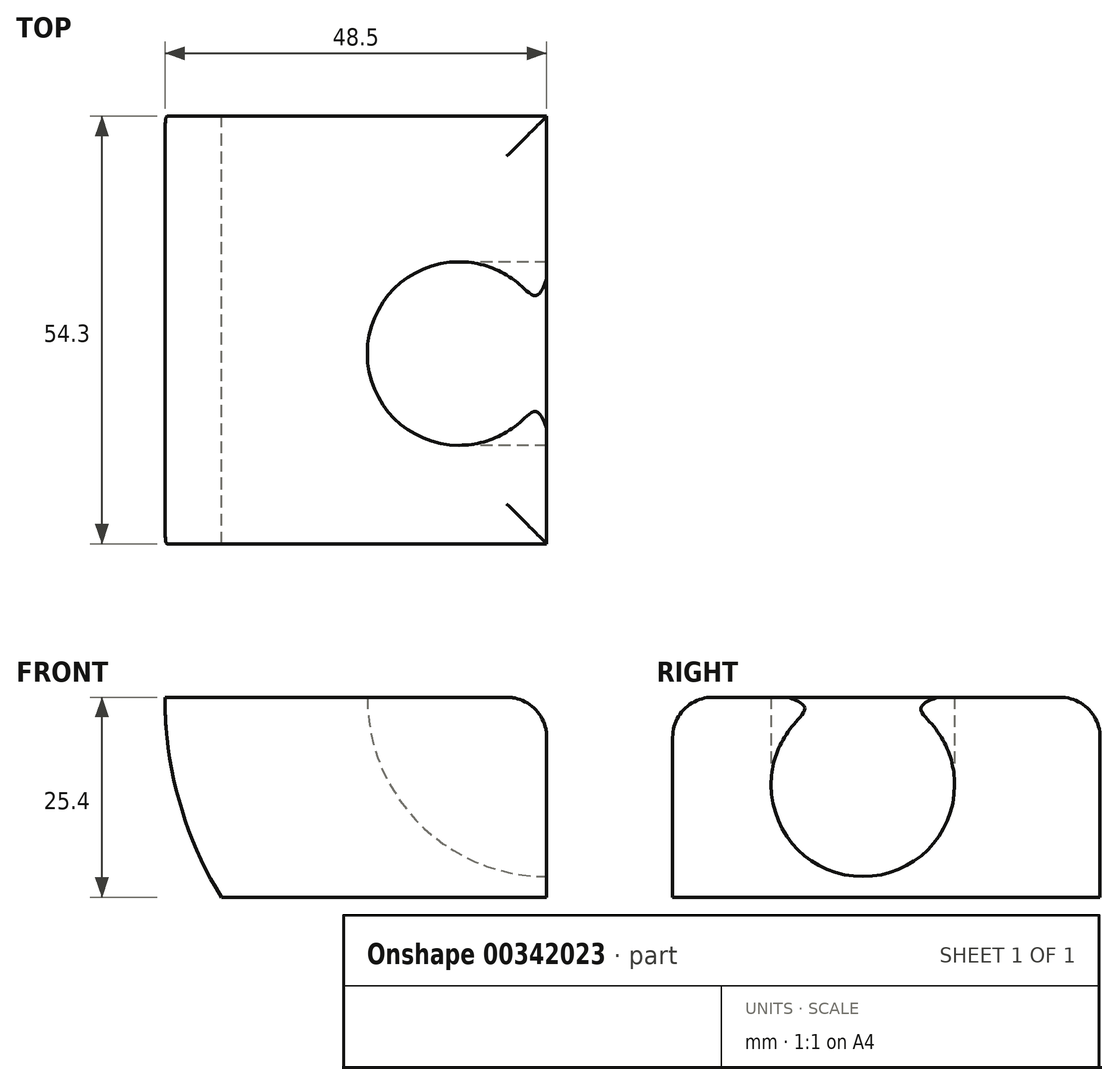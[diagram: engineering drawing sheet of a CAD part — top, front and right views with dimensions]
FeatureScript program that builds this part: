
annotation { "Feature Type Name" : "Feature", "Feature Type Description" : "" }
export const myFeature = defineFeature(function(context is Context, id is Id, definition is map)
    precondition{}
    {
        {
            var Q0;
            Q0=qCreatedBy(makeId("Top.planeOp"),FACE);
            var sketch = newSketch(context, id + "F0", { "sketchPlane" : qUnion([Q0])});
            skLineSegment(sketch, "E0.bottom", {"start": v(0, 0) * mm, "end": v(48.5, 0) * mm});
            skLineSegment(sketch, "E0.top", {"start": v(0, 54.3) * mm, "end": v(48.5, 54.3) * mm});
            skLineSegment(sketch, "E0.left", {"start": v(0, 0) * mm, "end": v(0, 54.3) * mm});
            skLineSegment(sketch, "E0.right", {"start": v(48.5, 0) * mm, "end": v(48.5, 54.3) * mm});
            skSolve(sketch);
        }
        {
            var Q0;
            Q0 = qSketchRegion(id + "F0", true);
            var Q1;
            Q1=makeQuery(id+"F0.imprint","IMPRINT",FACE,{"disambiguationData":[TD([[makeQuery(id+"F0.imprint","IMPRINT",EDGE,{"derivedFrom":sQuery(id+"F0.wireOp",EDGE,"E0.bottom")}),1.0]])]});
            extrude(context, id + "F1", {"entities" : qUnion([Q0, Q1]), "depth" : 25.4 * mm});
        }
        {
            var Q0;
            Q0=makeQuery(id+"F1.opExtrude","CAP_FACE",FACE,{"disambiguationData":[OSD([sQuery(id+"F0.wireOp",EDGE,"E0.bottom"),sQuery(id+"F0.wireOp",EDGE,"E0.top"),sQuery(id+"F0.wireOp",EDGE,"E0.left"),sQuery(id+"F0.wireOp",EDGE,"E0.right")])],"isStart":false});
            var sketch = newSketch(context, id + "F2", { "sketchPlane" : qUnion([Q0])});
            skCircle(sketch, "E1", {"center": v(37.37, 24.16) * mm, "radius": 11.65 * mm});
            skSolve(sketch);
        }
        {
            var Q0;
            {var subQ1=makeQuery(id+"F1.opExtrude","CAP_EDGE",EDGE,{"disambiguationData":[OSD([sQuery(id+"F0.wireOp",EDGE,"E0.bottom")])],"isStart":false});Q0=makeQuery(id+"F2.imprint","IMPRINT",FACE,{"disambiguationData":[TD([[makeQuery(id+"F2.imprint","IMPRINT",EDGE,{"derivedFrom":subQ1}),1.0]])]});}
            var Q1;
            Q1=makeQuery(id+"F1.opExtrude","CAP_EDGE",EDGE,{"disambiguationData":[OSD([sQuery(id+"F0.wireOp",EDGE,"E0.right")])],"isStart":false});
            revolve(context, id + "F3", {"operationType" : NewBodyOperationType.INTERSECT, "entities" : qUnion([Q0]), "axis" : qUnion([Q1]), "revolveType" : RevolveType.FULL, "oppositeDirection" : true});
        }
        {
            var Q0;
            Q0=makeQuery(id+"F1.opExtrude","CAP_EDGE",EDGE,{"disambiguationData":[OSD([sQuery(id+"F0.wireOp",EDGE,"E0.bottom")])],"isStart":false});
            var Q1;
            {var subQ0=sQuery(id+"F0.wireOp",EDGE,"E0.bottom");var subQ1=sQuery(id+"F0.wireOp",EDGE,"E0.right");Q1=makeQuery(id+"F3.boolean.opBoolean","SPLIT",EDGE,{"disambiguationData":[TD([makeQuery(id+"F1.opExtrude","SWEPT_FACE",FACE,{"disambiguationData":[OSD([subQ0])]})])],"derivedFrom":makeQuery(id+"F1.opExtrude","CAP_EDGE",EDGE,{"disambiguationData":[OSD([subQ1])],"isStart":false})});}
            var Q2;
            {var subQ0=sQuery(id+"F0.wireOp",EDGE,"E0.right");var subQ1=sQuery(id+"F0.wireOp",EDGE,"E0.top");Q2=makeQuery(id+"F3.boolean.opBoolean","SPLIT",EDGE,{"disambiguationData":[TD([makeQuery(id+"F1.opExtrude","SWEPT_FACE",FACE,{"disambiguationData":[OSD([subQ1])]})])],"derivedFrom":makeQuery(id+"F1.opExtrude","CAP_EDGE",EDGE,{"disambiguationData":[OSD([subQ0])],"isStart":false})});}
            var Q3;
            Q3=makeQuery(id+"F1.opExtrude","CAP_EDGE",EDGE,{"disambiguationData":[OSD([sQuery(id+"F0.wireOp",EDGE,"E0.top")])],"isStart":false});
            var Q4;
            Q4=makeQuery(id+"F1.opExtrude","CAP_EDGE",EDGE,{"disambiguationData":[OSD([sQuery(id+"F0.wireOp",EDGE,"E0.left")])],"isStart":false});
            fillet(context, id + "F4", {"entities" : qUnion([Q0, Q1, Q2, Q3, Q4]), "radius" : 5.08 * mm, "tangentPropagation" : true, "allowEdgeOverflow" : false});
        }
    });
